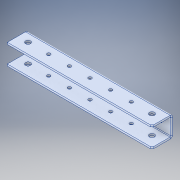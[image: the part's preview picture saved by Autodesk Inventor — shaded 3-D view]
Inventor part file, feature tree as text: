
AUTODESK INVENTOR PART (.ipt)
format: ipt  version: 2017 (Build 210142000, 142)  size: 259,584 bytes
history: native  units: in
note: dims shown in document units (in); Inventor stores cm internally (conversion verified against a paired STEP export)
features: sketch x2, split x1, hole x1, other x1
ambient origin geometry x8: Origin, YZ Plane, XZ Plane, XY Plane, X Axis, Y Axis, Z Axis, Center Point
bodies: Solid1 (feature_tree)
feature tree (5):
  split  "Split1"
  hole  "Hole1"  [1 undecoded]
  sketch  "Sketch1"  dims[d0=0.25in d1=0.25in]
  sketch  "Sketch2"  dims[d2=0.25in d3=0.75in d4=0.375in d5=0.25in d6=0.5635in d7=1.0in d8=0.8108in]
  other  "Break-Corner1"
note: 1 required parameter value undecoded (feature->parameter linkage not recoverable at this tier; creation-order binding heuristic only, values carry confidence <= 0.55)
